# Revit family: JC KONTAKTER JCK260 DE
name_source: partatom
category: Specialty Equipment
units: mm (PartAtom-declared; Revit-internal decimal feet)

## family parameters
Cut with Voids When Loaded = No
Enable Cutting in Views = Yes
Host = Face
Maintain Annotation Orientation = Yes
Part Type = Normal
Room Calculation Point = No
Round Connector Dimension = Use Diameter
Shared = No

## types (1)
- JCK260
    Anzahl der mikroschalter = 2
    CE-kennzeichnung = https://jckontakter.se
    Deckel = Aluminum ENAW 6060
    Deckel 2 = Aluminum ENAW 6060
    Default Elevation = 800 mm  [stored 2.62467 ft]
    Description = JCK260 ist nur 50 mm breit und wurde für die Montage an Glasflächen mit 50 mm Profilsystem sowie in anderen Bereichen entwickelt, in denen wenig Platz zur Verfügung steht. Das Modell verfügt über doppelte Druckflächen und ist aus silbereloxiertem Aluminium mit schwarzen Endkappen gefertigt. Beide Druckflächen sind mit taktilen Rillen versehen und dienen als zusätzliche Orientierungshilfe für sehbehinderte Personen. So lässt sich leicht erfühlen, wo man drücken muss, um die Türöffnung zu aktivieren.Unsere Großflächentaster mit doppelten Druckflächen sind für Umgebungen mit doppelten Schiebetüren entwickelt und ermöglichen es, jede Tür separat mit einem eigenen Druckknopf zu steuern. Diese Funktion trägt dazu bei, Zugluft und Kaltluft zu reduzieren und spart Energie im Vergleich dazu, dass beide Türen bei jeder Öffnung aufgefahren werden. Diese Armbogenkontakte können auch in einem Durchgang geeignet sein, wo es zwei Eingänge zum Raum gibt.
    Endkappen = POM Tenac C 4520
    Geringster nennstrom = 1mA/4 V DC
    Herstellungsland = Schweden
    Kern = Aluminum ENAW 6060
    Kunststoffstück = POM Tenac C 4520
    Manufacturer = JC kontakter
    Mikroschalter = Standard NO IP67
    Model = JCK260
    Nomineller nennstrom = 12 V - Resistive 6A Inductive L/R 5ms 6A, 24 V - Resistive 6A Inductive L/R 5ms 5A
    Produktgewicht = 0.341 kg.
    Technisches Produktblatt = https://grossflaechentaster.de
    URL = https://grossflaechentaster.de

note: [stored X ft] marks values corroborated as IEEE doubles in the binary element streams (Revit-internal decimal feet)

## geometry (parser evidence)
native form markers: Sweep x6
no freeform markers — native parametric forms only
